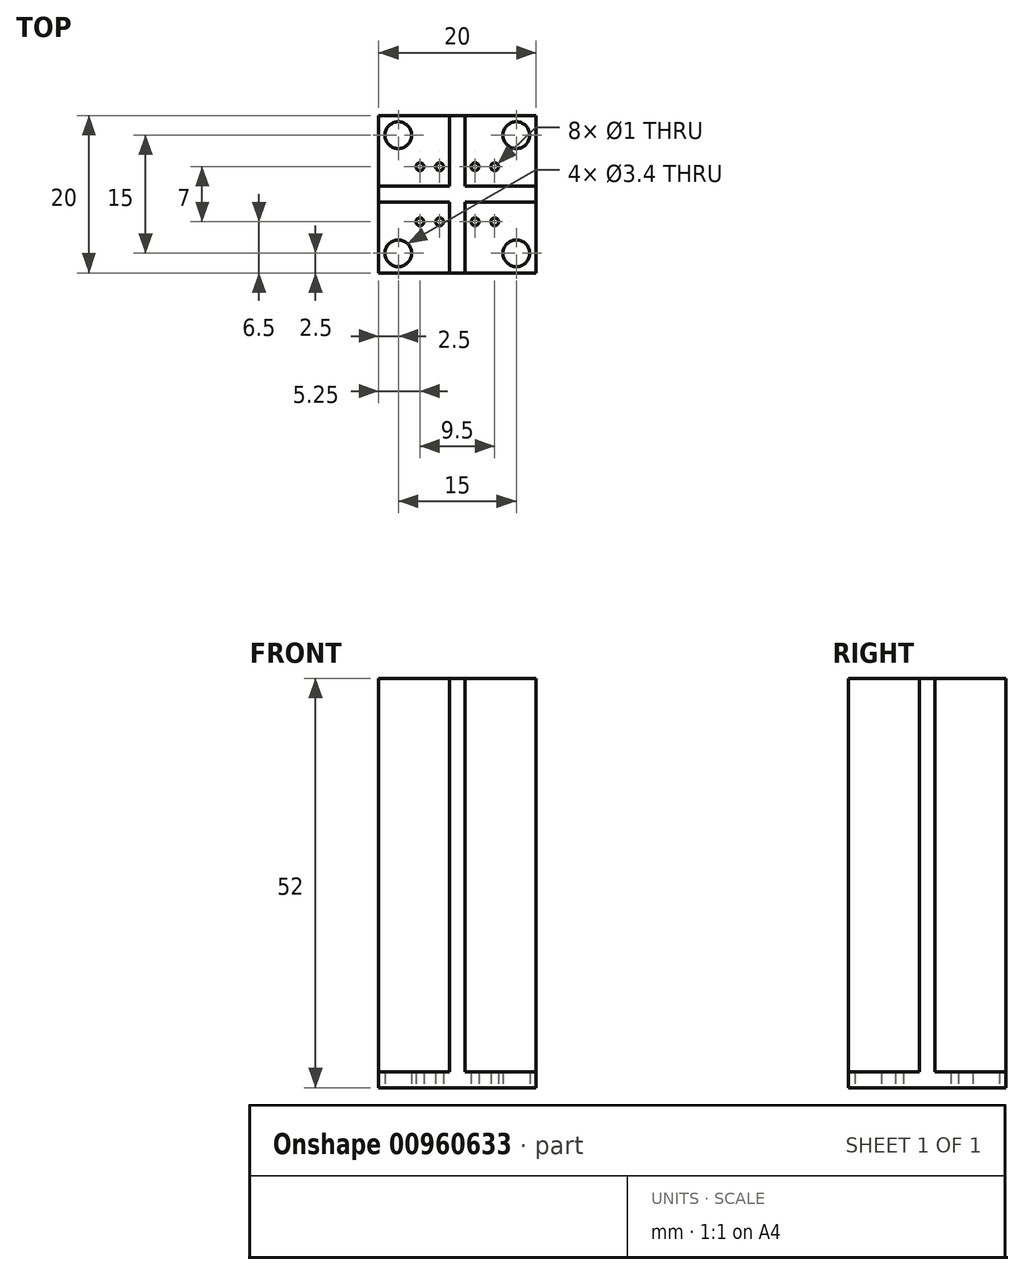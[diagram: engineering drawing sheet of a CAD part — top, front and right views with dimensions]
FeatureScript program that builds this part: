
annotation { "Feature Type Name" : "Feature", "Feature Type Description" : "" }
export const myFeature = defineFeature(function(context is Context, id is Id, definition is map)
    precondition{}
    {
        {
            var Q0;
            Q0=qCreatedBy(makeId("Top.planeOp"),FACE);
            var sketch = newSketch(context, id + "F0", { "sketchPlane" : qUnion([Q0])});
            skLineSegment(sketch, "E0.bottom", {"start": v(10, 10) * mm, "end": v(-10, 10) * mm});
            skLineSegment(sketch, "E0.top", {"start": v(10, -10) * mm, "end": v(-10, -10) * mm});
            skLineSegment(sketch, "E0.left", {"start": v(10, 10) * mm, "end": v(10, -10) * mm});
            skLineSegment(sketch, "E0.right", {"start": v(-10, 10) * mm, "end": v(-10, -10) * mm});
            skPoint(sketch, "E0.middle", {"position": v(0, 0) * mm});
            skLineSegment(sketch, "E1.bottom", {"start": v(-1, 10) * mm, "end": v(1, 10) * mm});
            skLineSegment(sketch, "E1.top", {"start": v(-1, -10) * mm, "end": v(1, -10) * mm});
            skLineSegment(sketch, "E2.left", {"start": v(-10, 1) * mm, "end": v(-10, -1) * mm});
            skLineSegment(sketch, "E2.right", {"start": v(10, 1) * mm, "end": v(10, -1) * mm});
            skLineSegment(sketch, "E3", {"start": v(-10, 0) * mm, "end": v(10, 0) * mm, "construction": true});
            skLineSegment(sketch, "E4", {"start": v(0, 10) * mm, "end": v(0, -10) * mm, "construction": true});
            skLineSegment(sketch, "E5.bottom", {"start": v(-1, 10) * mm, "end": v(1, 10) * mm, "construction": true});
            skLineSegment(sketch, "E5.top", {"start": v(-1, -10) * mm, "end": v(1, -10) * mm, "construction": true});
            skLineSegment(sketch, "E5.left", {"start": v(-1, 10) * mm, "end": v(-1, -10) * mm, "construction": true});
            skLineSegment(sketch, "E5.right", {"start": v(1, 10) * mm, "end": v(1, -10) * mm, "construction": true});
            skLineSegment(sketch, "E6.bottom", {"start": v(-10, 1) * mm, "end": v(10, 1) * mm, "construction": true});
            skLineSegment(sketch, "E6.top", {"start": v(-10, -1) * mm, "end": v(10, -1) * mm, "construction": true});
            skLineSegment(sketch, "E6.left", {"start": v(-10, 1) * mm, "end": v(-10, -1) * mm, "construction": true});
            skLineSegment(sketch, "E6.right", {"start": v(10, 1) * mm, "end": v(10, -1) * mm, "construction": true});
            skCircle(sketch, "E7", {"center": v(-3.5, 3.5) * mm, "radius": 2.5 * mm, "construction": true});
            skPoint(sketch, "E8", {"position": v(-2.25, 3.5) * mm});
            skPoint(sketch, "E9", {"position": v(-4.75, 3.5) * mm});
            skPoint(sketch, "E10.MirrorP", {"position": v(-2.25, -3.5) * mm});
            skPoint(sketch, "E11.MirrorP", {"position": v(-4.75, -3.5) * mm});
            skPoint(sketch, "E12.MirrorP", {"position": v(2.25, 3.5) * mm});
            skPoint(sketch, "E13.MirrorP", {"position": v(4.75, 3.5) * mm});
            skPoint(sketch, "E14.MirrorP", {"position": v(4.75, -3.5) * mm});
            skPoint(sketch, "E15.MirrorP", {"position": v(2.25, -3.5) * mm});
            skSolve(sketch);
        }
        {
            var Q0;
            Q0 = qSketchRegion(id + "F0", true);
            var Q1;
            {var subQ0=sQuery(id+"F0.wireOp",EDGE,"E2.bottom");var subQ1=sQuery(id+"F0.wireOp",EDGE,"E1.left");var subQ2=makeQuery(id+"F0.imprint","INTERSECT",VERTEX,{"derivedFrom":[subQ1,subQ0]});Q1=makeQuery(id+"F0.imprint","IMPRINT",FACE,{"disambiguationData":[TD([[makeQuery(id+"F0.imprint","IMPRINT",EDGE,{"disambiguationData":[TD([[subQ2,-1.0]])],"derivedFrom":subQ1}),1.0]])]});}
            extrude(context, id + "F1", {"entities" : qUnion([Q0, Q1]), "depth" : 2 * mm, "offsetDistance" : 25 * mm, "symmetric" : true});
        }
        {
            var Q0;
            Q0=makeQuery(id+"F1.opExtrude","CAP_FACE",FACE,{"disambiguationData":[OSD([sQuery(id+"F0.wireOp",EDGE,"E0.bottom"),sQuery(id+"F0.wireOp",EDGE,"E0.top"),sQuery(id+"F0.wireOp",EDGE,"E0.left"),sQuery(id+"F0.wireOp",EDGE,"E0.right"),sQuery(id+"F0.wireOp",EDGE,"E1.bottom"),sQuery(id+"F0.wireOp",EDGE,"E1.top"),sQuery(id+"F0.wireOp",EDGE,"E2.left"),sQuery(id+"F0.wireOp",EDGE,"E2.right")])],"isStart":false});
            var sketch = newSketch(context, id + "F2", { "sketchPlane" : qUnion([Q0])});
            skLineSegment(sketch, "E16", {"start": v(0, 10) * mm, "end": v(0, -10) * mm, "construction": true});
            skLineSegment(sketch, "E17", {"start": v(-10, 0) * mm, "end": v(10, 0) * mm, "construction": true});
            skPoint(sketch, "E18", {"position": v(-3.5, 3.5) * mm});
            skPoint(sketch, "E19", {"position": v(-4.75, 3.5) * mm});
            skPoint(sketch, "E20", {"position": v(-2.25, 3.5) * mm});
            skPoint(sketch, "E21.MirrorP", {"position": v(-4.75, -3.5) * mm});
            skPoint(sketch, "E22.MirrorP", {"position": v(-2.25, -3.5) * mm});
            skPoint(sketch, "E23.MirrorP", {"position": v(2.25, 3.5) * mm});
            skPoint(sketch, "E24.MirrorP", {"position": v(4.75, 3.5) * mm});
            skPoint(sketch, "E25.MirrorP", {"position": v(4.75, -3.5) * mm});
            skPoint(sketch, "E26.MirrorP", {"position": v(2.25, -3.5) * mm});
            skSolve(sketch);
        }
        {
            var Q0;
            Q0=sQuery(id+"F2.wireOp",VERTEX,"E19");
            var Q1;
            Q1=sQuery(id+"F2.wireOp",VERTEX,"E20");
            var Q2;
            Q2=sQuery(id+"F2.wireOp",VERTEX,"E21.MirrorP");
            var Q3;
            Q3=sQuery(id+"F2.wireOp",VERTEX,"E22.MirrorP");
            var Q4;
            Q4=sQuery(id+"F2.wireOp",VERTEX,"E23.MirrorP");
            var Q5;
            Q5=sQuery(id+"F2.wireOp",VERTEX,"E24.MirrorP");
            var Q6;
            Q6=sQuery(id+"F2.wireOp",VERTEX,"E25.MirrorP");
            var Q7;
            Q7=sQuery(id+"F2.wireOp",VERTEX,"E26.MirrorP");
            var Q8;
            Q8=makeQuery(id+"F1.opExtrude","SWEPT_BODY",BODY,{"disambiguationData":[OSD([sQuery(id+"F0.wireOp",EDGE,"E0.bottom"),sQuery(id+"F0.wireOp",EDGE,"E0.top"),sQuery(id+"F0.wireOp",EDGE,"E0.left"),sQuery(id+"F0.wireOp",EDGE,"E0.right"),sQuery(id+"F0.wireOp",EDGE,"E1.bottom"),sQuery(id+"F0.wireOp",EDGE,"E1.top"),sQuery(id+"F0.wireOp",EDGE,"E2.left"),sQuery(id+"F0.wireOp",EDGE,"E2.right")])]});
            hole(context, id + "F3", {"style" : HoleStyle.SIMPLE, "endStyle" : HoleEndStyle.THROUGH, "standardTappedOrClearance" : lookupTablePath({ "standard" : "ISO", "size" : "1", "type" : "Drilled" }), "standardBlindInLast" : lookupTablePath({ "standard" : "ISO", "size" : "1", "type" : "Drilled" }), "holeDiameter" : 1 * mm, "majorDiameter" : 5 * mm, "isTappedThrough" : true, "tappedDepth" : 18.5 * mm, "tapClearance" : 3, "locations" : qUnion([Q0, Q1, Q2, Q3, Q4, Q5, Q6, Q7]), "scope" : qUnion([Q8]), "startStyle" : HoleStartStyle.PART});
        }
        {
            var Q0;
            Q0=makeQuery(id+"F1.opExtrude","CAP_FACE",FACE,{"disambiguationData":[OSD([sQuery(id+"F0.wireOp",EDGE,"E0.bottom"),sQuery(id+"F0.wireOp",EDGE,"E0.top"),sQuery(id+"F0.wireOp",EDGE,"E0.left"),sQuery(id+"F0.wireOp",EDGE,"E0.right"),sQuery(id+"F0.wireOp",EDGE,"E1.bottom"),sQuery(id+"F0.wireOp",EDGE,"E1.top"),sQuery(id+"F0.wireOp",EDGE,"E2.left"),sQuery(id+"F0.wireOp",EDGE,"E2.right")])],"isStart":false});
            var sketch = newSketch(context, id + "F4", { "sketchPlane" : qUnion([Q0])});
            skLineSegment(sketch, "E27.bottom", {"start": v(-1, 10) * mm, "end": v(1, 10) * mm});
            skLineSegment(sketch, "E27.top", {"start": v(-1, -10) * mm, "end": v(1, -10) * mm});
            skLineSegment(sketch, "E27.left", {"start": v(-1, 10) * mm, "end": v(-1, -10) * mm});
            skLineSegment(sketch, "E27.right", {"start": v(1, 10) * mm, "end": v(1, -10) * mm});
            skLineSegment(sketch, "E28.bottom", {"start": v(-10, 1) * mm, "end": v(10, 1) * mm});
            skLineSegment(sketch, "E28.top", {"start": v(-10, -1) * mm, "end": v(10, -1) * mm});
            skLineSegment(sketch, "E28.left", {"start": v(-10, 1) * mm, "end": v(-10, -1) * mm});
            skLineSegment(sketch, "E28.right", {"start": v(10, 1) * mm, "end": v(10, -1) * mm});
            skPoint(sketch, "E29", {"position": v(-7.5, 7.5) * mm});
            skLineSegment(sketch, "E30", {"start": v(0, 10) * mm, "end": v(0, -10) * mm, "construction": true});
            skLineSegment(sketch, "E31", {"start": v(-10, 0) * mm, "end": v(10, 0) * mm, "construction": true});
            skPoint(sketch, "E32.MirrorP", {"position": v(7.5, 7.5) * mm});
            skPoint(sketch, "E33.MirrorP", {"position": v(-7.5, -7.5) * mm});
            skPoint(sketch, "E34.MirrorP", {"position": v(7.5, -7.5) * mm});
            skSolve(sketch);
        }
        {
            var Q0;
            Q0 = qSketchRegion(id + "F4", true);
            extrude(context, id + "F5", {"entities" : qUnion([Q0]), "operationType" : NewBodyOperationType.ADD, "depth" : 50 * mm, "offsetDistance" : 25 * mm});
        }
        {
            var Q0;
            Q0=sQuery(id+"F4.wireOp",VERTEX,"E29");
            var Q1;
            Q1=sQuery(id+"F4.wireOp",VERTEX,"E32.MirrorP");
            var Q2;
            Q2=sQuery(id+"F4.wireOp",VERTEX,"E34.MirrorP");
            var Q3;
            Q3=sQuery(id+"F4.wireOp",VERTEX,"E33.MirrorP");
            var Q4;
            Q4=makeQuery(id+"F1.opExtrude","SWEPT_BODY",BODY,{"disambiguationData":[OSD([sQuery(id+"F0.wireOp",EDGE,"E0.bottom"),sQuery(id+"F0.wireOp",EDGE,"E0.top"),sQuery(id+"F0.wireOp",EDGE,"E0.left"),sQuery(id+"F0.wireOp",EDGE,"E0.right"),sQuery(id+"F0.wireOp",EDGE,"E1.bottom"),sQuery(id+"F0.wireOp",EDGE,"E1.top"),sQuery(id+"F0.wireOp",EDGE,"E2.left"),sQuery(id+"F0.wireOp",EDGE,"E2.right")])]});
            hole(context, id + "F6", {"style" : HoleStyle.SIMPLE, "endStyle" : HoleEndStyle.THROUGH, "standardTappedOrClearance" : lookupTablePath({ "fit" : "Normal", "standard" : "ISO", "size" : "M3", "type" : "Clearance" }), "standardBlindInLast" : lookupTablePath({ "fit" : "Normal", "standard" : "ISO", "engagement" : "75%", "pitch" : "0.5 mm", "size" : "M3", "type" : "Clearance & tapped" }), "holeDiameter" : 3.4 * mm, "majorDiameter" : 5 * mm, "isTappedThrough" : true, "tappedDepth" : 18.5 * mm, "tapClearance" : 3, "locations" : qUnion([Q0, Q1, Q2, Q3]), "scope" : qUnion([Q4]), "startStyle" : HoleStartStyle.PART});
        }
    });
